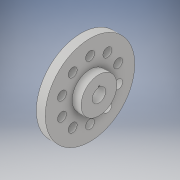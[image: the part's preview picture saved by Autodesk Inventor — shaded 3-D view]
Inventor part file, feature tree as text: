
AUTODESK INVENTOR PART (.ipt)
format: ipt  version: 2018 (Build 220112000, 112)  size: 157,696 bytes
history: native  units: in
note: dims shown in document units (in); Inventor stores cm internally (conversion verified against a paired STEP export)
features: sketch x3, revolve x1, extrude x1, hole x1
ambient origin geometry x8: Origin, YZ Plane, XZ Plane, XY Plane, X Axis, Y Axis, Z Axis, Center Point
bodies: Solid1 (feature_tree)
feature tree (6):
  revolve  "Revolution1"  [1 undecoded]
  extrude  "Extrusion1"  Depth=1.0in
  hole  "Hole3"  [1 undecoded]
  sketch  "Sketch1"  dims[d0=0.5in d1=2.125in]
  sketch  "Sketch3"  dims[d4=1.0in d5=0.625in]
  sketch  "Sketch7"  dims[d6=0.375in d7=90.0deg d9=0.05in d10=0.05in d11=1.0in d12=0.0in d29=1.65in d30=3.937in d32=360.0deg d34=0.5in d35=0.75in d36=0.375in d37=0.25in d38=0.5635in d39=1.0in d40=0.8108in d14=1.0in d15=1.0in]
note: 2 required parameter values undecoded (feature->parameter linkage not recoverable at this tier; creation-order binding heuristic only, values carry confidence <= 0.55)